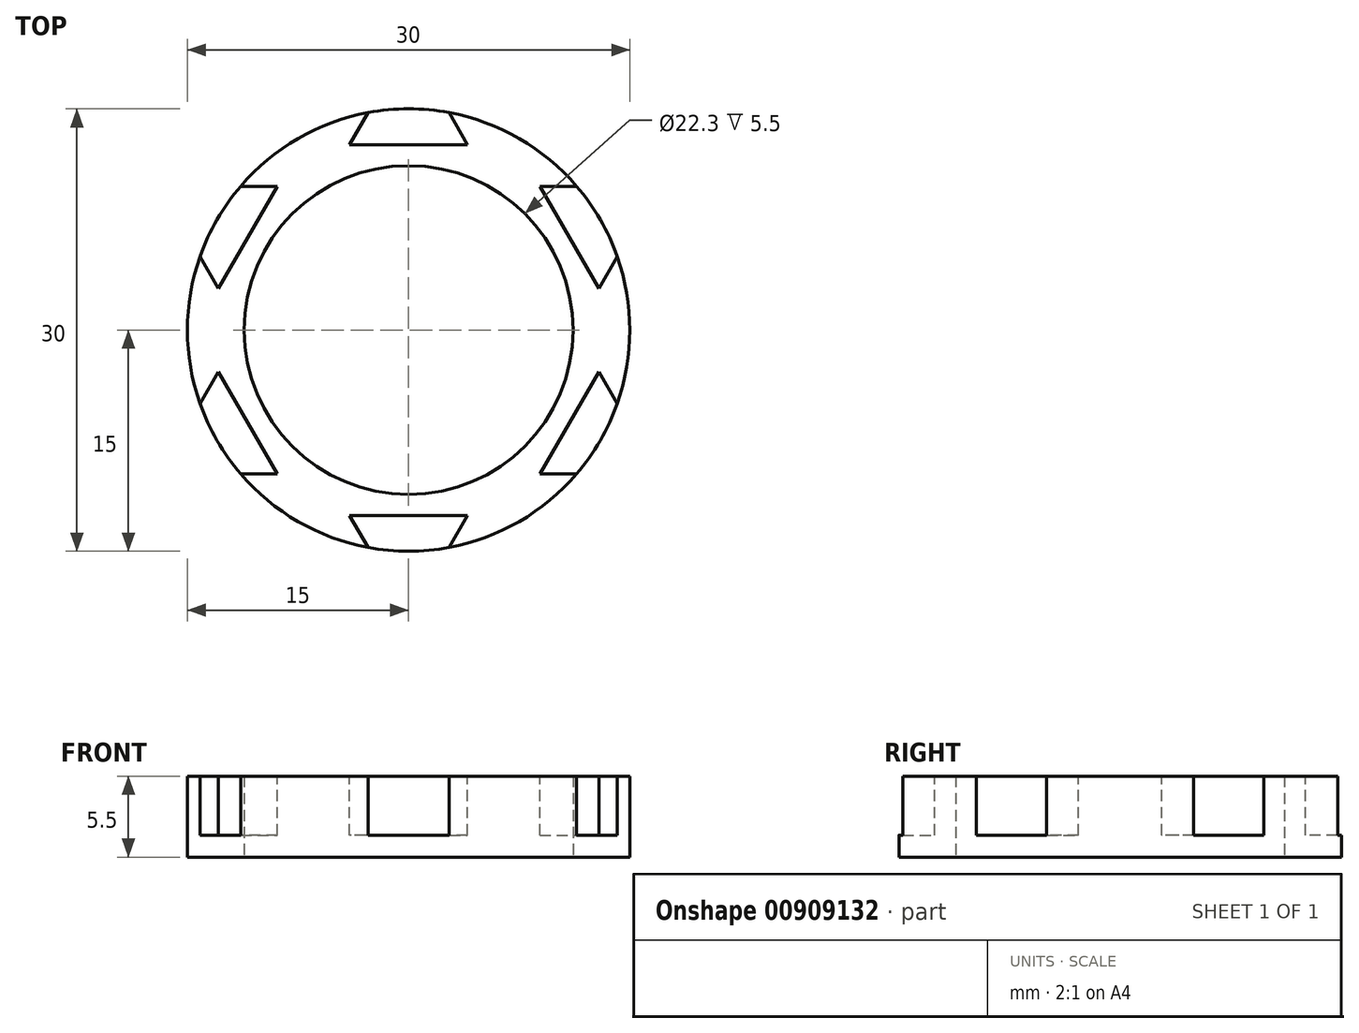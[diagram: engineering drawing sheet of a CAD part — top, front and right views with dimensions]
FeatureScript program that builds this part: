
annotation { "Feature Type Name" : "Feature", "Feature Type Description" : "" }
export const myFeature = defineFeature(function(context is Context, id is Id, definition is map)
    precondition{}
    {
        {
            var Q0;
            Q0=qCreatedBy(makeId("Top.planeOp"),FACE);
            var sketch = newSketch(context, id + "F0", { "sketchPlane" : qUnion([Q0])});
            skCircle(sketch, "E0", {"center": v(0, 0) * mm, "radius": 11.15 * mm});
            skCircle(sketch, "E1", {"center": v(0, 0) * mm, "radius": 15 * mm});
            skLineSegment(sketch, "E2", {"start": v(-2.75, 14.75) * mm, "end": v(-4, 12.58) * mm});
            skLineSegment(sketch, "E3", {"start": v(-4, 12.58) * mm, "end": v(0, 12.58) * mm});
            skLineSegment(sketch, "E4.MirrorCS", {"start": v(4, 12.58) * mm, "end": v(0, 12.58) * mm});
            skLineSegment(sketch, "E5.MirrorCS", {"start": v(2.75, 14.75) * mm, "end": v(4, 12.58) * mm});
            skSolve(sketch);
        }
        {
            var Q0;
            Q0=makeQuery(id+"F0.imprint","IMPRINT",FACE,{"disambiguationData":[TD([[makeQuery(id+"F0.imprint","IMPRINT",EDGE,{"derivedFrom":sQuery(id+"F0.wireOp",EDGE,"E0")}),-1.0]])]});
            var Q1;
            {var subQ0=sQuery(id+"F0.wireOp",EDGE,"E2");Q1=makeQuery(id+"F0.imprint","IMPRINT",FACE,{"disambiguationData":[TD([[makeQuery(id+"F0.imprint","IMPRINT",EDGE,{"derivedFrom":subQ0}),1.0]])]});}
            extrude(context, id + "F1", {"entities" : qUnion([Q0, Q1]), "depth" : 4 * mm, "offsetDistance" : 25 * mm});
        }
        {
            var Q0;
            Q0=makeQuery(id+"F1.opExtrude","CAP_FACE",FACE,{"disambiguationData":[OSD([sQuery(id+"F0.wireOp",EDGE,"E0"),sQuery(id+"F0.wireOp",EDGE,"E1"),sQuery(id+"F0.wireOp",EDGE,"E2"),sQuery(id+"F0.wireOp",EDGE,"E3"),sQuery(id+"F0.wireOp",EDGE,"E4.MirrorCS"),sQuery(id+"F0.wireOp",EDGE,"E5.MirrorCS")])],"isStart":false});
            var sketch = newSketch(context, id + "F2", { "sketchPlane" : qUnion([Q0])});
            skPoint(sketch, "E6", {"position": v(14.15, 5) * mm});
            skPoint(sketch, "E7", {"position": v(12.9, 2.83) * mm});
            skPoint(sketch, "E8", {"position": v(8.9, 9.75) * mm});
            skPoint(sketch, "E9", {"position": v(11.4, 9.75) * mm});
            skPoint(sketch, "E10.MirrorP", {"position": v(-8.9, 9.75) * mm});
            skPoint(sketch, "E11.MirrorP", {"position": v(-12.9, 2.83) * mm});
            skPoint(sketch, "E12.MirrorP", {"position": v(-14.15, 5) * mm});
            skPoint(sketch, "E13.MirrorP", {"position": v(-11.4, 9.75) * mm});
            skPoint(sketch, "E14.MirrorP", {"position": v(-12.9, -2.83) * mm});
            skPoint(sketch, "E15.MirrorP", {"position": v(-14.15, -5) * mm});
            skPoint(sketch, "E16.MirrorP", {"position": v(-11.4, -9.75) * mm});
            skPoint(sketch, "E17.MirrorP", {"position": v(-8.9, -9.75) * mm});
            skPoint(sketch, "E18.MirrorP", {"position": v(12.9, -2.83) * mm});
            skPoint(sketch, "E19.MirrorP", {"position": v(8.9, -9.75) * mm});
            skPoint(sketch, "E20.MirrorP", {"position": v(11.4, -9.75) * mm});
            skPoint(sketch, "E21.MirrorP", {"position": v(14.15, -5) * mm});
            skPoint(sketch, "E22", {"position": v(-4, 12.58) * mm});
            skPoint(sketch, "E23", {"position": v(-2.75, 14.75) * mm});
            skPoint(sketch, "E24", {"position": v(2.75, 14.75) * mm});
            skPoint(sketch, "E25", {"position": v(4, 12.58) * mm});
            skPoint(sketch, "E26.MirrorP", {"position": v(-4, -12.58) * mm});
            skPoint(sketch, "E27.MirrorP", {"position": v(-2.75, -14.75) * mm});
            skPoint(sketch, "E28.MirrorP", {"position": v(4, -12.58) * mm});
            skPoint(sketch, "E29.MirrorP", {"position": v(2.75, -14.75) * mm});
            skLineSegment(sketch, "E30", {"start": v(-14.15, 5) * mm, "end": v(-12.9, 2.83) * mm});
            skLineSegment(sketch, "E31", {"start": v(-8.9, 9.75) * mm, "end": v(-12.9, 2.83) * mm});
            skLineSegment(sketch, "E32", {"start": v(-11.4, 9.75) * mm, "end": v(-8.9, 9.75) * mm});
            skLineSegment(sketch, "E33", {"start": v(-12.9, -2.83) * mm, "end": v(-8.9, -9.75) * mm});
            skLineSegment(sketch, "E34", {"start": v(-11.4, -9.75) * mm, "end": v(-8.9, -9.75) * mm});
            skLineSegment(sketch, "E35", {"start": v(-14.15, -5) * mm, "end": v(-12.9, -2.83) * mm});
            skLineSegment(sketch, "E36", {"start": v(-2.75, -14.75) * mm, "end": v(-4, -12.58) * mm});
            skLineSegment(sketch, "E37", {"start": v(4, -12.58) * mm, "end": v(-4, -12.58) * mm});
            skLineSegment(sketch, "E38", {"start": v(2.75, -14.75) * mm, "end": v(4, -12.58) * mm});
            skLineSegment(sketch, "E39", {"start": v(8.9, -9.75) * mm, "end": v(11.4, -9.75) * mm});
            skLineSegment(sketch, "E40", {"start": v(8.9, -9.75) * mm, "end": v(12.9, -2.83) * mm});
            skLineSegment(sketch, "E41", {"start": v(14.15, -5) * mm, "end": v(12.9, -2.83) * mm});
            skLineSegment(sketch, "E42", {"start": v(14.15, 5) * mm, "end": v(12.9, 2.83) * mm});
            skLineSegment(sketch, "E43", {"start": v(8.9, 9.75) * mm, "end": v(12.9, 2.83) * mm});
            skLineSegment(sketch, "E44", {"start": v(11.4, 9.75) * mm, "end": v(8.9, 9.75) * mm});
            skLineSegment(sketch, "E45", {"start": v(-2.75, 14.75) * mm, "end": v(-4, 12.58) * mm});
            skLineSegment(sketch, "E46", {"start": v(4, 12.58) * mm, "end": v(2.75, 14.75) * mm});
            skLineSegment(sketch, "E47", {"start": v(-4, 12.58) * mm, "end": v(4, 12.58) * mm});
            skSolve(sketch);
        }
        {
            var Q0;
            {var subQ0=sQuery(id+"F2.wireOp",EDGE,"E30");Q0=makeQuery(id+"F2.imprint","IMPRINT",FACE,{"disambiguationData":[TD([[makeQuery(id+"F2.imprint","IMPRINT",EDGE,{"derivedFrom":subQ0}),1.0]])]});}
            var Q1;
            Q1=makeQuery(id+"F2.imprint","IMPRINT",FACE,{"disambiguationData":[TD([[makeQuery(id+"F2.imprint","IMPRINT",EDGE,{"derivedFrom":sQuery(id+"F2.wireOp",EDGE,"E33")}),-1.0]])]});
            var Q2;
            {var subQ0=sQuery(id+"F2.wireOp",EDGE,"E36");Q2=makeQuery(id+"F2.imprint","IMPRINT",FACE,{"disambiguationData":[TD([[makeQuery(id+"F2.imprint","IMPRINT",EDGE,{"derivedFrom":subQ0}),-1.0]])]});}
            var Q3;
            {var subQ0=sQuery(id+"F2.wireOp",EDGE,"E39");Q3=makeQuery(id+"F2.imprint","IMPRINT",FACE,{"disambiguationData":[TD([[makeQuery(id+"F2.imprint","IMPRINT",EDGE,{"derivedFrom":subQ0}),1.0]])]});}
            var Q4;
            {var subQ0=sQuery(id+"F2.wireOp",EDGE,"E42");Q4=makeQuery(id+"F2.imprint","IMPRINT",FACE,{"disambiguationData":[TD([[makeQuery(id+"F2.imprint","IMPRINT",EDGE,{"derivedFrom":subQ0}),-1.0]])]});}
            var Q5;
            {var subQ0=sQuery(id+"F2.wireOp",EDGE,"E45");Q5=makeQuery(id+"F2.imprint","IMPRINT",FACE,{"disambiguationData":[TD([[makeQuery(id+"F2.imprint","IMPRINT",EDGE,{"derivedFrom":subQ0}),1.0]])]});}
            extrude(context, id + "F3", {"entities" : qUnion([Q0, Q1, Q2, Q3, Q4, Q5]), "operationType" : NewBodyOperationType.REMOVE, "oppositeDirection" : true, "depth" : 16.2 * mm, "offsetDistance" : 25 * mm});
        }
        {
            var Q0;
            Q0=makeQuery(id+"F1.opExtrude","CAP_FACE",FACE,{"disambiguationData":[OSD([sQuery(id+"F0.wireOp",EDGE,"E0"),sQuery(id+"F0.wireOp",EDGE,"E1")])],"isStart":true});
            var sketch = newSketch(context, id + "F4", { "sketchPlane" : qUnion([Q0])});
            skCircle(sketch, "E48", {"center": v(0, 0) * mm, "radius": 15 * mm});
            skCircle(sketch, "E49", {"center": v(0, 0) * mm, "radius": 11.15 * mm});
            skSolve(sketch);
        }
        {
            var Q0;
            Q0=makeQuery(id+"F4.imprint","IMPRINT",FACE,{"disambiguationData":[TD([[makeQuery(id+"F4.imprint","IMPRINT",EDGE,{"derivedFrom":sQuery(id+"F4.wireOp",EDGE,"E49")}),1.0]])]});
            var Q1;
            {var subQ1=makeQuery(id+"F1.opExtrude","CAP_FACE",FACE,{"disambiguationData":[OSD([sQuery(id+"F0.wireOp",EDGE,"E0"),sQuery(id+"F0.wireOp",EDGE,"E1")])],"isStart":true});var subQ6=makeQuery(id+"F3.boolean.opBoolean","INTERSECT",EDGE,{"derivedFrom":[subQ1,makeQuery(id+"F3.opExtrude","SWEPT_FACE",FACE,{"disambiguationData":[OSD([sQuery(id+"F2.wireOp",EDGE,"E43")])]})]});Q1=makeQuery(id+"F4.imprint","IMPRINT",FACE,{"disambiguationData":[TD([[makeQuery(id+"F4.imprint","IMPRINT",EDGE,{"derivedFrom":subQ6}),-1.0]])]});}
            var Q2;
            {var subQ1=makeQuery(id+"F1.opExtrude","CAP_FACE",FACE,{"disambiguationData":[OSD([sQuery(id+"F0.wireOp",EDGE,"E0"),sQuery(id+"F0.wireOp",EDGE,"E1")])],"isStart":true});var subQ6=makeQuery(id+"F3.boolean.opBoolean","INTERSECT",EDGE,{"derivedFrom":[subQ1,makeQuery(id+"F3.opExtrude","SWEPT_FACE",FACE,{"disambiguationData":[OSD([sQuery(id+"F2.wireOp",EDGE,"E37")])]})]});Q2=makeQuery(id+"F4.imprint","IMPRINT",FACE,{"disambiguationData":[TD([[makeQuery(id+"F4.imprint","IMPRINT",EDGE,{"derivedFrom":subQ6}),-1.0]])]});}
            var Q3;
            {var subQ1=makeQuery(id+"F1.opExtrude","CAP_FACE",FACE,{"disambiguationData":[OSD([sQuery(id+"F0.wireOp",EDGE,"E0"),sQuery(id+"F0.wireOp",EDGE,"E1")])],"isStart":true});var subQ6=makeQuery(id+"F3.boolean.opBoolean","INTERSECT",EDGE,{"derivedFrom":[subQ1,makeQuery(id+"F3.opExtrude","SWEPT_FACE",FACE,{"disambiguationData":[OSD([sQuery(id+"F2.wireOp",EDGE,"E31")])]})]});Q3=makeQuery(id+"F4.imprint","IMPRINT",FACE,{"disambiguationData":[TD([[makeQuery(id+"F4.imprint","IMPRINT",EDGE,{"derivedFrom":subQ6}),1.0]])]});}
            var Q4;
            {var subQ1=makeQuery(id+"F1.opExtrude","CAP_FACE",FACE,{"disambiguationData":[OSD([sQuery(id+"F0.wireOp",EDGE,"E0"),sQuery(id+"F0.wireOp",EDGE,"E1")])],"isStart":true});var subQ6=makeQuery(id+"F3.boolean.opBoolean","INTERSECT",EDGE,{"derivedFrom":[subQ1,makeQuery(id+"F3.opExtrude","SWEPT_FACE",FACE,{"disambiguationData":[OSD([sQuery(id+"F2.wireOp",EDGE,"E40")])]})]});Q4=makeQuery(id+"F4.imprint","IMPRINT",FACE,{"disambiguationData":[TD([[makeQuery(id+"F4.imprint","IMPRINT",EDGE,{"derivedFrom":subQ6}),1.0]])]});}
            var Q5;
            {var subQ1=makeQuery(id+"F1.opExtrude","CAP_FACE",FACE,{"disambiguationData":[OSD([sQuery(id+"F0.wireOp",EDGE,"E0"),sQuery(id+"F0.wireOp",EDGE,"E1")])],"isStart":true});var subQ6=makeQuery(id+"F3.boolean.opBoolean","INTERSECT",EDGE,{"derivedFrom":[subQ1,makeQuery(id+"F3.opExtrude","SWEPT_FACE",FACE,{"disambiguationData":[OSD([sQuery(id+"F2.wireOp",EDGE,"E33")])]})]});Q5=makeQuery(id+"F4.imprint","IMPRINT",FACE,{"disambiguationData":[TD([[makeQuery(id+"F4.imprint","IMPRINT",EDGE,{"derivedFrom":subQ6}),1.0]])]});}
            var Q6;
            {var subQ1=makeQuery(id+"F1.opExtrude","CAP_FACE",FACE,{"disambiguationData":[OSD([sQuery(id+"F0.wireOp",EDGE,"E0"),sQuery(id+"F0.wireOp",EDGE,"E1")])],"isStart":true});var subQ6=makeQuery(id+"F3.boolean.opBoolean","INTERSECT",EDGE,{"derivedFrom":[subQ1,makeQuery(id+"F3.opExtrude","SWEPT_FACE",FACE,{"disambiguationData":[OSD([sQuery(id+"F2.wireOp",EDGE,"E47")])]})]});Q6=makeQuery(id+"F4.imprint","IMPRINT",FACE,{"disambiguationData":[TD([[makeQuery(id+"F4.imprint","IMPRINT",EDGE,{"derivedFrom":subQ6}),-1.0]])]});}
            extrude(context, id + "F5", {"entities" : qUnion([Q0, Q1, Q2, Q3, Q4, Q5, Q6]), "operationType" : NewBodyOperationType.ADD, "depth" : 1.5 * mm, "offsetDistance" : 25 * mm});
        }
    });
